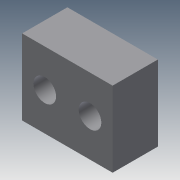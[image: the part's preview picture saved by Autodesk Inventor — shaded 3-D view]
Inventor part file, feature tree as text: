
AUTODESK INVENTOR PART (.ipt)
format: ipt  version: 2013 (Build 170138000, 138)  size: 89,600 bytes
history: native  units: mm
features: extrude x2, sketch x2
ambient origin geometry x8: Origin, YZ Plane, XZ Plane, XY Plane, X Axis, Y Axis, Z Axis, Center Point
bodies: Solid1 (feature_tree)
feature tree (4):
  extrude  "Extrusion1"  Depth=10.0mm
  extrude  "Extrusion2"  Depth=3.0mm
  sketch  "Sketch1"  dims[d0=12.0mm d1=10.0mm]
  sketch  "Sketch2"  dims[d2=6.0mm d3=0.0mm d4=3.0mm d5=3.0mm d6=3.0mm d7=3.0mm d8=6.0mm d9=0.0mm]
